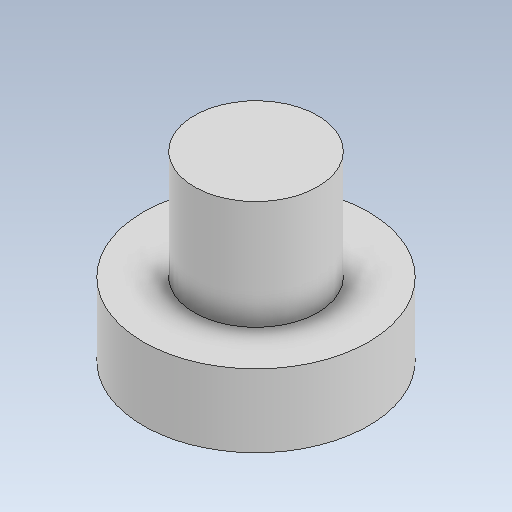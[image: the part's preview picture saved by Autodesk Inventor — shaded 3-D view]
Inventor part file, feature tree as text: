
AUTODESK INVENTOR PART (.ipt)
format: ipt  version: 2020 (Build 240168000, 168)  size: 104,448 bytes
history: native  units: mm
features: extrude x2, sketch x2
ambient origin geometry x8: Origin, YZ Plane, XZ Plane, XY Plane, X Axis, Y Axis, Z Axis, Center Point
bodies: Solid1 (feature_tree)
feature tree (4):
  extrude  "Extrusion1"  Depth=2.5mm TaperAngle=0.0deg
  extrude  "Extrusion2"  Depth=3.75mm TaperAngle=0.0deg
  sketch  "Sketch1"  dims[d0=7.75mm d2=2.5mm d3=0.0mm]
  sketch  "Sketch2"  dims[d4=4.25mm d5=3.75mm d6=0.0mm]
